# Revit family: VUT_VUE 270 V5B_Eng
name_source: partatom
category: Mechanical Equipment
units: mm (PartAtom-declared; Revit-internal decimal feet)

## family parameters
Always vertical = Yes
Classification = None
Cut with Voids When Loaded = No
Part Type = Normal
Room Calculation Point = No
Round Connector Dimension = Use Diameter
Shared = No
Work Plane-Based = No

## types (2) — shared parameters
00_20_Manufacturer = Vents
00_20_Name = Heat recovery air handling unit
Amperage = 1 A
Casing Material = Polypropylene (black)
Diameter = 125 mm  [stored 0.410105 ft]
Filter = G4
Height = 893 mm  [stored 2.92979 ft]
Length = 590 mm  [stored 1.9357 ft]
Load Classification = HVAC
Maintenance zone material = <By Category>
Manufacturer = Vents
Maximum Air Flow = 300.0 m³/h
Number of Fase = 1
Power = 162 W
Sound pressure level at 3 m distance = 34 dBA
URL = https://ventilation-system.com
Voltage = 230 V
Width = 316 mm
zero-valued in all types: Default Elevation

## per-type parameters (varying)
| type | Weight |
| VUT 270 V5B EC A21 | 13.00 kg |
| VUE 270 V5B EC A21 | 13.50 kg |

note: column(s) folded — value = type name in every type: 00_20_Type

note: [stored X ft] marks values corroborated as IEEE doubles in the binary element streams (Revit-internal decimal feet)
